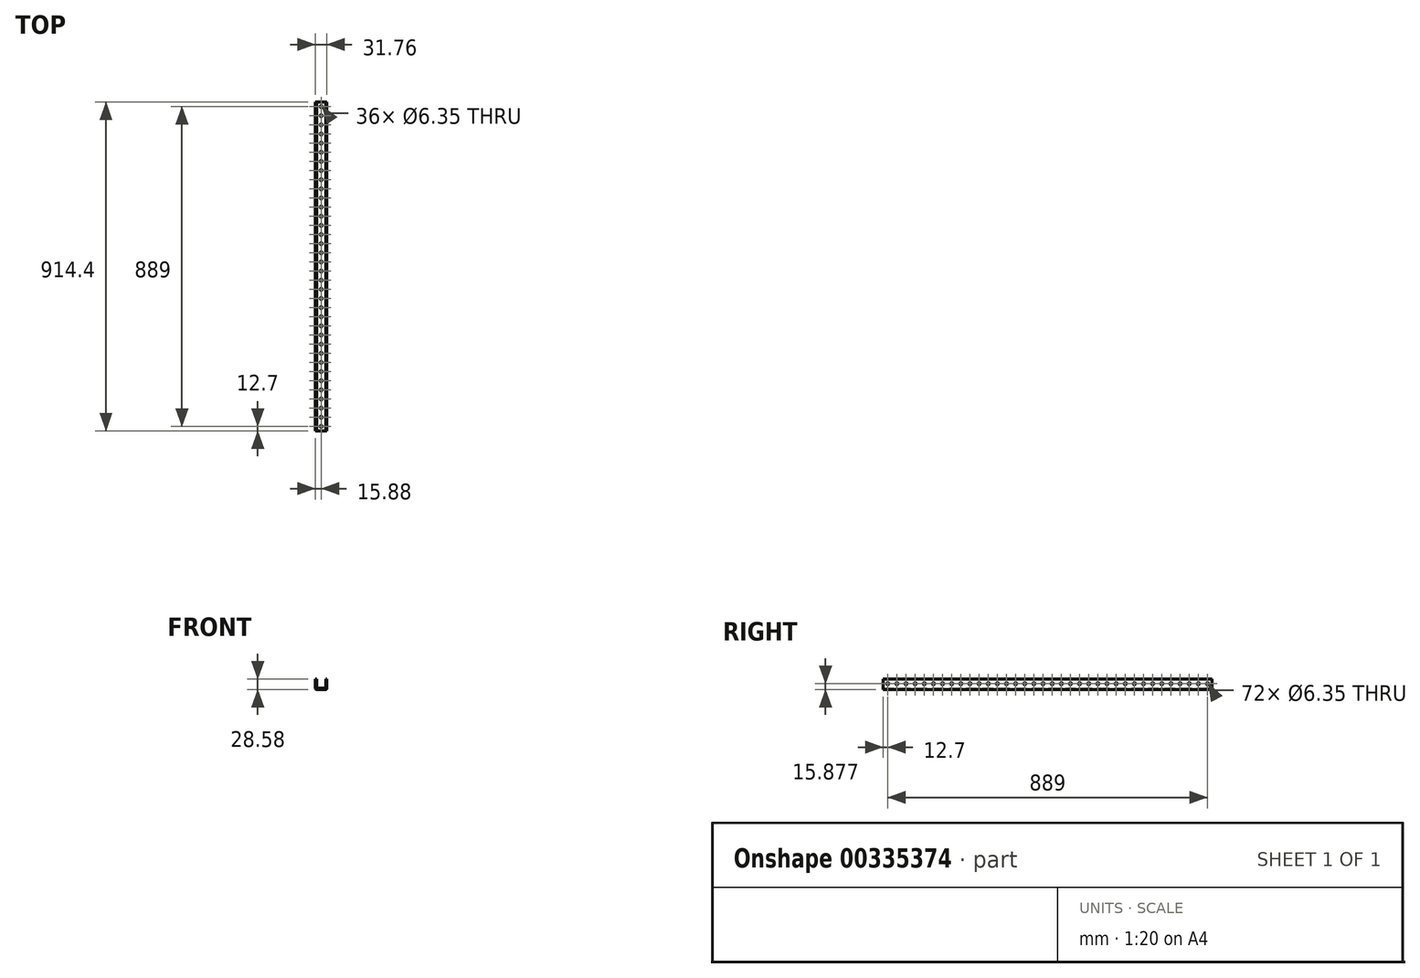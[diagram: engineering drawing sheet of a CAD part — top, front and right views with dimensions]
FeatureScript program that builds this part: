
annotation { "Feature Type Name" : "Feature", "Feature Type Description" : "" }
export const myFeature = defineFeature(function(context is Context, id is Id, definition is map)
    precondition{}
    {
        {
            var Q0;
            Q0=qCreatedBy(makeId("Front.planeOp"),FACE);
            var sketch = newSketch(context, id + "F0", { "sketchPlane" : qUnion([Q0])});
            skLineSegment(sketch, "E0.bottom", {"start": v(12.7, -14.29) * mm, "end": v(-12.7, -14.29) * mm});
            skLineSegment(sketch, "E0.left", {"start": v(15.88, -11.11) * mm, "end": v(15.87, 14.29) * mm});
            skLineSegment(sketch, "E0.right", {"start": v(-15.87, -11.11) * mm, "end": v(-15.88, 14.29) * mm});
            skPoint(sketch, "E0.middle", {"position": v(0, 0) * mm});
            skLineSegment(sketch, "E1", {"start": v(-12.7, 14.29) * mm, "end": v(-12.7, -11.11) * mm});
            skLineSegment(sketch, "E2", {"start": v(-12.7, -11.11) * mm, "end": v(12.7, -11.11) * mm});
            skLineSegment(sketch, "E3", {"start": v(12.7, -11.11) * mm, "end": v(12.7, 14.29) * mm});
            skLineSegment(sketch, "E4", {"start": v(-15.88, 14.29) * mm, "end": v(-12.7, 14.29) * mm});
            skLineSegment(sketch, "E5", {"start": v(12.7, 14.29) * mm, "end": v(15.87, 14.29) * mm});
            skPoint(sketch, "E6.visualSharp", {"position": v(-15.87, -14.29) * mm});
            skArc(sketch, "E6.filletArc", {"start": v(-15.87, -11.11) * mm, "mid": v(-14.95, -13.36) * mm, "end": v(-12.7, -14.29) * mm});
            skPoint(sketch, "E7.visualSharp", {"position": v(15.88, -14.29) * mm});
            skArc(sketch, "E7.filletArc", {"start": v(12.7, -14.29) * mm, "mid": v(14.95, -13.36) * mm, "end": v(15.88, -11.11) * mm});
            skSolve(sketch);
        }
        {
            var Q0;
            Q0 = qSketchRegion(id + "F0", true);
            extrude(context, id + "F1", {"entities" : qUnion([Q0]), "depth" : 914.4 * mm});
        }
        {
            var Q0;
            Q0=makeQuery(id+"F1.opExtrude","SWEPT_FACE",FACE,{"disambiguationData":[OSD([sQuery(id+"F0.wireOp",EDGE,"E0.bottom")])]});
            var sketch = newSketch(context, id + "F2", { "sketchPlane" : qUnion([Q0])});
            skCircle(sketch, "E8", {"center": v(0, 12.7) * mm, "radius": 3.18 * mm});
            skCircle(sketch, "E9.0.1.0", {"center": v(0, 38.1) * mm, "radius": 3.18 * mm});
            skCircle(sketch, "E9.0.2.0", {"center": v(0, 63.5) * mm, "radius": 3.18 * mm});
            skCircle(sketch, "E9.0.3.0", {"center": v(0, 88.9) * mm, "radius": 3.18 * mm});
            skCircle(sketch, "E9.0.4.0", {"center": v(0, 114.3) * mm, "radius": 3.18 * mm});
            skCircle(sketch, "E9.0.5.0", {"center": v(0, 139.7) * mm, "radius": 3.18 * mm});
            skCircle(sketch, "E9.0.6.0", {"center": v(0, 165.1) * mm, "radius": 3.18 * mm});
            skCircle(sketch, "E9.0.7.0", {"center": v(0, 190.5) * mm, "radius": 3.18 * mm});
            skCircle(sketch, "E9.0.8.0", {"center": v(0, 215.9) * mm, "radius": 3.18 * mm});
            skCircle(sketch, "E9.0.9.0", {"center": v(0, 241.3) * mm, "radius": 3.18 * mm});
            skCircle(sketch, "E9.0.10.0", {"center": v(0, 266.7) * mm, "radius": 3.18 * mm});
            skCircle(sketch, "E9.0.11.0", {"center": v(0, 292.1) * mm, "radius": 3.18 * mm});
            skCircle(sketch, "E9.0.12.0", {"center": v(0, 317.5) * mm, "radius": 3.18 * mm});
            skCircle(sketch, "E9.0.13.0", {"center": v(0, 342.9) * mm, "radius": 3.18 * mm});
            skCircle(sketch, "E9.0.14.0", {"center": v(0, 368.3) * mm, "radius": 3.18 * mm});
            skCircle(sketch, "E9.0.15.0", {"center": v(0, 393.7) * mm, "radius": 3.18 * mm});
            skCircle(sketch, "E9.0.16.0", {"center": v(0, 419.1) * mm, "radius": 3.18 * mm});
            skCircle(sketch, "E9.0.17.0", {"center": v(0, 444.5) * mm, "radius": 3.18 * mm});
            skCircle(sketch, "E9.0.18.0", {"center": v(0, 469.9) * mm, "radius": 3.18 * mm});
            skCircle(sketch, "E9.0.19.0", {"center": v(0, 495.3) * mm, "radius": 3.18 * mm});
            skCircle(sketch, "E9.0.20.0", {"center": v(0, 520.7) * mm, "radius": 3.18 * mm});
            skCircle(sketch, "E9.0.21.0", {"center": v(0, 546.1) * mm, "radius": 3.18 * mm});
            skCircle(sketch, "E9.0.22.0", {"center": v(0, 571.5) * mm, "radius": 3.18 * mm});
            skCircle(sketch, "E9.0.23.0", {"center": v(0, 596.9) * mm, "radius": 3.18 * mm});
            skCircle(sketch, "E9.0.24.0", {"center": v(0, 622.3) * mm, "radius": 3.18 * mm});
            skCircle(sketch, "E9.0.25.0", {"center": v(0, 647.7) * mm, "radius": 3.18 * mm});
            skCircle(sketch, "E9.0.26.0", {"center": v(0, 673.1) * mm, "radius": 3.18 * mm});
            skCircle(sketch, "E9.0.27.0", {"center": v(0, 698.5) * mm, "radius": 3.18 * mm});
            skCircle(sketch, "E9.0.28.0", {"center": v(0, 723.9) * mm, "radius": 3.18 * mm});
            skCircle(sketch, "E9.0.29.0", {"center": v(0, 749.3) * mm, "radius": 3.18 * mm});
            skCircle(sketch, "E9.0.30.0", {"center": v(0, 774.7) * mm, "radius": 3.18 * mm});
            skCircle(sketch, "E9.0.31.0", {"center": v(0, 800.1) * mm, "radius": 3.18 * mm});
            skCircle(sketch, "E9.0.32.0", {"center": v(0, 825.5) * mm, "radius": 3.18 * mm});
            skCircle(sketch, "E9.0.33.0", {"center": v(0, 850.9) * mm, "radius": 3.18 * mm});
            skCircle(sketch, "E9.0.34.0", {"center": v(0, 876.3) * mm, "radius": 3.18 * mm});
            skCircle(sketch, "E9.0.35.0", {"center": v(0, 901.7) * mm, "radius": 3.18 * mm});
            skLineSegment(sketch, "E9.direction1", {"start": v(0, 12.7) * mm, "end": v(25.4, 12.7) * mm, "construction": true});
            skLineSegment(sketch, "E9.direction2", {"start": v(0, 12.7) * mm, "end": v(0, 38.1) * mm, "construction": true});
            skSolve(sketch);
        }
        {
            var Q0;
            Q0 = qSketchRegion(id + "F2", true);
            extrude(context, id + "F3", {"entities" : qUnion([Q0]), "operationType" : NewBodyOperationType.REMOVE, "endBound" : BoundingType.THROUGH_ALL, "oppositeDirection" : true, "depth" : 25.4 * mm});
        }
        {
            var Q0;
            Q0=makeQuery(id+"F1.opExtrude","SWEPT_FACE",FACE,{"disambiguationData":[OSD([sQuery(id+"F0.wireOp",EDGE,"E0.right")])]});
            var sketch = newSketch(context, id + "F4", { "sketchPlane" : qUnion([Q0])});
            skCircle(sketch, "E10", {"center": v(12.7, 1.59) * mm, "radius": 3.18 * mm});
            skCircle(sketch, "E11.0.1.0", {"center": v(38.1, 1.59) * mm, "radius": 3.18 * mm});
            skCircle(sketch, "E11.0.2.0", {"center": v(63.5, 1.59) * mm, "radius": 3.18 * mm});
            skCircle(sketch, "E11.0.3.0", {"center": v(88.9, 1.59) * mm, "radius": 3.18 * mm});
            skCircle(sketch, "E11.0.4.0", {"center": v(114.3, 1.59) * mm, "radius": 3.18 * mm});
            skCircle(sketch, "E11.0.5.0", {"center": v(139.7, 1.59) * mm, "radius": 3.18 * mm});
            skCircle(sketch, "E11.0.6.0", {"center": v(165.1, 1.59) * mm, "radius": 3.18 * mm});
            skCircle(sketch, "E11.0.7.0", {"center": v(190.5, 1.59) * mm, "radius": 3.18 * mm});
            skCircle(sketch, "E11.0.8.0", {"center": v(215.9, 1.59) * mm, "radius": 3.18 * mm});
            skCircle(sketch, "E11.0.9.0", {"center": v(241.3, 1.59) * mm, "radius": 3.18 * mm});
            skCircle(sketch, "E11.0.10.0", {"center": v(266.7, 1.59) * mm, "radius": 3.18 * mm});
            skCircle(sketch, "E11.0.11.0", {"center": v(292.1, 1.59) * mm, "radius": 3.18 * mm});
            skCircle(sketch, "E11.0.12.0", {"center": v(317.5, 1.59) * mm, "radius": 3.18 * mm});
            skCircle(sketch, "E11.0.13.0", {"center": v(342.9, 1.59) * mm, "radius": 3.18 * mm});
            skCircle(sketch, "E11.0.14.0", {"center": v(368.3, 1.59) * mm, "radius": 3.18 * mm});
            skCircle(sketch, "E11.0.15.0", {"center": v(393.7, 1.59) * mm, "radius": 3.18 * mm});
            skCircle(sketch, "E11.0.16.0", {"center": v(419.1, 1.59) * mm, "radius": 3.18 * mm});
            skCircle(sketch, "E11.0.17.0", {"center": v(444.5, 1.59) * mm, "radius": 3.18 * mm});
            skCircle(sketch, "E11.0.18.0", {"center": v(469.9, 1.59) * mm, "radius": 3.18 * mm});
            skCircle(sketch, "E11.0.19.0", {"center": v(495.3, 1.59) * mm, "radius": 3.18 * mm});
            skCircle(sketch, "E11.0.20.0", {"center": v(520.7, 1.59) * mm, "radius": 3.18 * mm});
            skCircle(sketch, "E11.0.21.0", {"center": v(546.1, 1.59) * mm, "radius": 3.18 * mm});
            skCircle(sketch, "E11.0.22.0", {"center": v(571.5, 1.59) * mm, "radius": 3.18 * mm});
            skCircle(sketch, "E11.0.23.0", {"center": v(596.9, 1.59) * mm, "radius": 3.18 * mm});
            skCircle(sketch, "E11.0.24.0", {"center": v(622.3, 1.59) * mm, "radius": 3.18 * mm});
            skCircle(sketch, "E11.0.25.0", {"center": v(647.7, 1.59) * mm, "radius": 3.18 * mm});
            skCircle(sketch, "E11.0.26.0", {"center": v(673.1, 1.59) * mm, "radius": 3.18 * mm});
            skCircle(sketch, "E11.0.27.0", {"center": v(698.5, 1.59) * mm, "radius": 3.18 * mm});
            skCircle(sketch, "E11.0.28.0", {"center": v(723.9, 1.59) * mm, "radius": 3.18 * mm});
            skCircle(sketch, "E11.0.29.0", {"center": v(749.3, 1.59) * mm, "radius": 3.18 * mm});
            skCircle(sketch, "E11.0.30.0", {"center": v(774.7, 1.59) * mm, "radius": 3.18 * mm});
            skCircle(sketch, "E11.0.31.0", {"center": v(800.1, 1.59) * mm, "radius": 3.18 * mm});
            skCircle(sketch, "E11.0.32.0", {"center": v(825.5, 1.59) * mm, "radius": 3.18 * mm});
            skCircle(sketch, "E11.0.33.0", {"center": v(850.9, 1.59) * mm, "radius": 3.18 * mm});
            skCircle(sketch, "E11.0.34.0", {"center": v(876.3, 1.59) * mm, "radius": 3.18 * mm});
            skCircle(sketch, "E11.0.35.0", {"center": v(901.7, 1.59) * mm, "radius": 3.18 * mm});
            skLineSegment(sketch, "E11.direction1", {"start": v(12.7, 1.59) * mm, "end": v(12.7, -23.81) * mm, "construction": true});
            skLineSegment(sketch, "E11.direction2", {"start": v(12.7, 1.59) * mm, "end": v(38.1, 1.59) * mm, "construction": true});
            skSolve(sketch);
        }
        {
            var Q0;
            Q0 = qSketchRegion(id + "F4", true);
            extrude(context, id + "F5", {"entities" : qUnion([Q0]), "operationType" : NewBodyOperationType.REMOVE, "endBound" : BoundingType.THROUGH_ALL, "oppositeDirection" : true, "depth" : 25.4 * mm});
        }
    });
